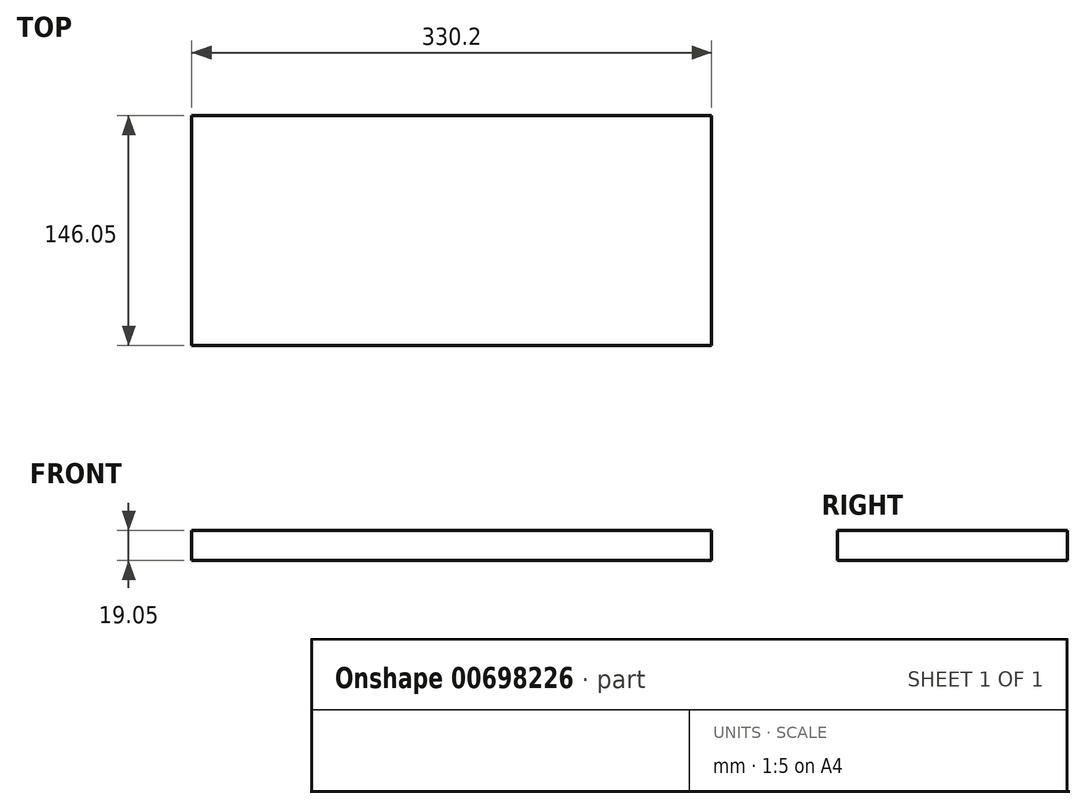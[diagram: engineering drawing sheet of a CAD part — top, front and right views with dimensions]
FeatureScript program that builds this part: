
annotation { "Feature Type Name" : "Feature", "Feature Type Description" : "" }
export const myFeature = defineFeature(function(context is Context, id is Id, definition is map)
    precondition{}
    {
        {
            var Q0;
            Q0=qCreatedBy(makeId("Top.planeOp"),FACE);
            var sketch = newSketch(context, id + "F0", { "sketchPlane" : qUnion([Q0])});
            skLineSegment(sketch, "E0.bottom", {"start": v(-258.73, -107.04) * mm, "end": v(71.47, -107.04) * mm});
            skLineSegment(sketch, "E0.top", {"start": v(-258.73, -253.09) * mm, "end": v(71.47, -253.09) * mm});
            skLineSegment(sketch, "E0.left", {"start": v(-258.73, -107.04) * mm, "end": v(-258.73, -253.09) * mm});
            skLineSegment(sketch, "E0.right", {"start": v(71.47, -107.04) * mm, "end": v(71.47, -253.09) * mm});
            skSolve(sketch);
        }
        {
            var Q0;
            Q0=makeQuery(id+"F0.imprint","IMPRINT",FACE,{"disambiguationData":[TD([[makeQuery(id+"F0.imprint","IMPRINT",EDGE,{"derivedFrom":sQuery(id+"F0.wireOp",EDGE,"E0.bottom")}),-1.0]])]});
            extrude(context, id + "F1", {"entities" : qUnion([Q0]), "depth" : 19.05 * mm, "offsetDistance" : 25.4 * mm});
        }
    });
